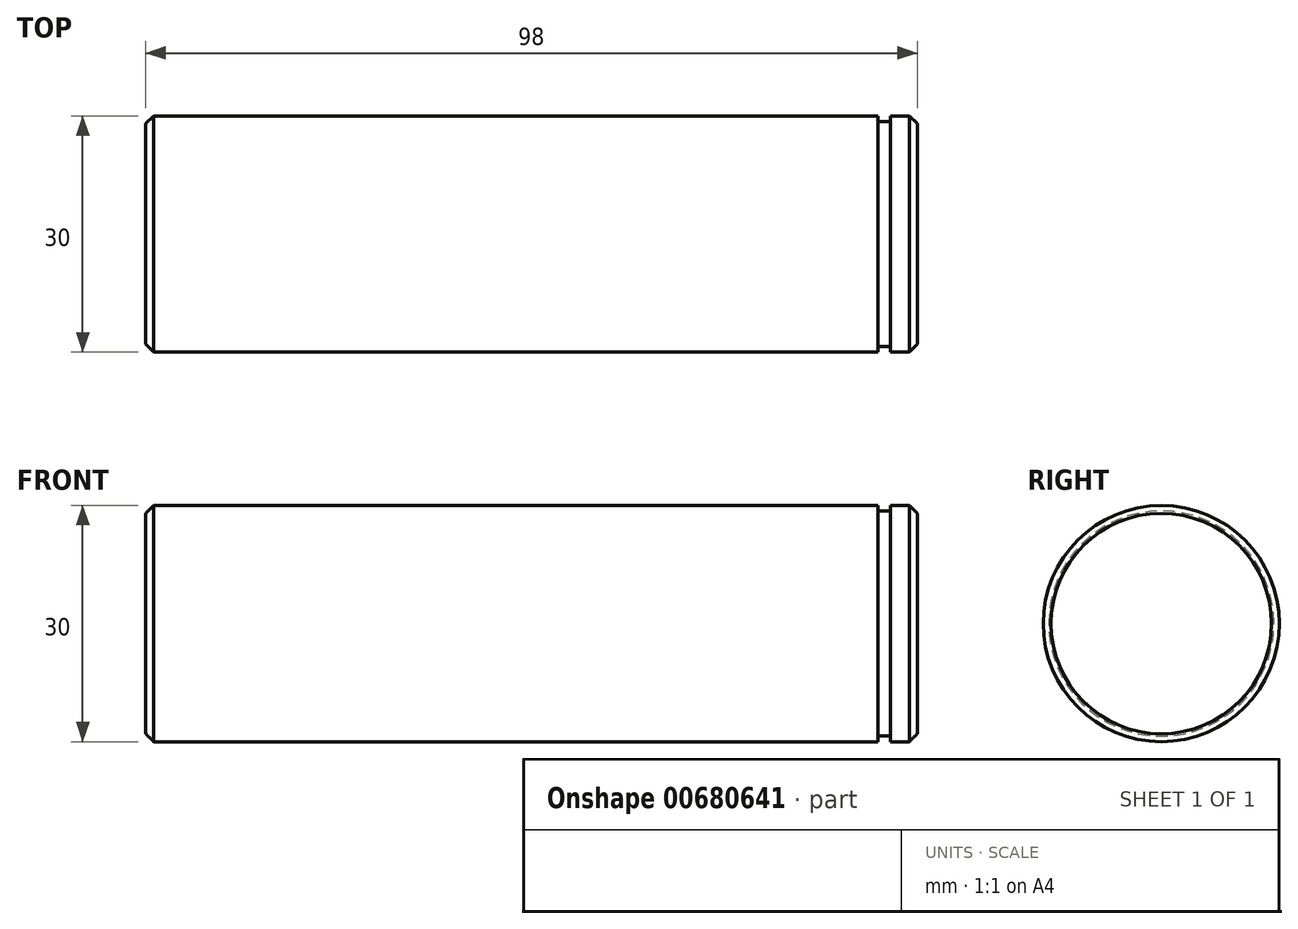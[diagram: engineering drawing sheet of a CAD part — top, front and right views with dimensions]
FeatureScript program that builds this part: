
annotation { "Feature Type Name" : "Feature", "Feature Type Description" : "" }
export const myFeature = defineFeature(function(context is Context, id is Id, definition is map)
    precondition{}
    {
        {
            var Q0;
            Q0=qCreatedBy(makeId("Right.planeOp"),FACE);
            var sketch = newSketch(context, id + "F0", { "sketchPlane" : qUnion([Q0])});
            skCircle(sketch, "E0", {"center": v(0, 0) * mm, "radius": 15 * mm});
            skSolve(sketch);
        }
        {
            var Q0;
            Q0 = qSketchRegion(id + "F0", true);
            extrude(context, id + "F1", {"entities" : qUnion([Q0]), "endBound" : BoundingType.SYMMETRIC, "depth" : 98 * mm, "offsetDistance" : 25 * mm});
        }
        {
            var Q0;
            Q0=qCreatedBy(makeId("Right.planeOp"),FACE);
            cPlane(context, id + "F2", {"entities" : qUnion([Q0]), "cplaneType" : CPlaneType.OFFSET, "offset" : 44 * mm, "width" : 150 * mm, "height" : 150 * mm});
        }
        {
            var Q0;
            Q0=qCreatedBy(id+"F2.planeOp",FACE);
            var sketch = newSketch(context, id + "F3", { "sketchPlane" : qUnion([Q0])});
            skCircle(sketch, "E1", {"center": v(0, 0) * mm, "radius": 14.3 * mm});
            skCircle(sketch, "E2", {"center": v(0, 0) * mm, "radius": 17.96 * mm});
            skSolve(sketch);
        }
        {
            var Q0;
            Q0 = qSketchRegion(id + "F3", true);
            extrude(context, id + "F4", {"entities" : qUnion([Q0]), "operationType" : NewBodyOperationType.REMOVE, "depth" : 1.6 * mm, "offsetDistance" : 25 * mm});
        }
        {
            var Q0;
            Q0=makeQuery(id+"F1.opExtrude","CAP_EDGE",EDGE,{"disambiguationData":[OSD([sQuery(id+"F0.wireOp",EDGE,"E0")])],"isStart":true});
            var Q1;
            Q1=makeQuery(id+"F1.opExtrude","CAP_EDGE",EDGE,{"disambiguationData":[OSD([sQuery(id+"F0.wireOp",EDGE,"E0")])],"isStart":false});
            chamfer(context, id + "F5", {"entities" : qUnion([Q0, Q1]), "width" : 1 * mm, "tangentPropagation" : true});
        }
    });
